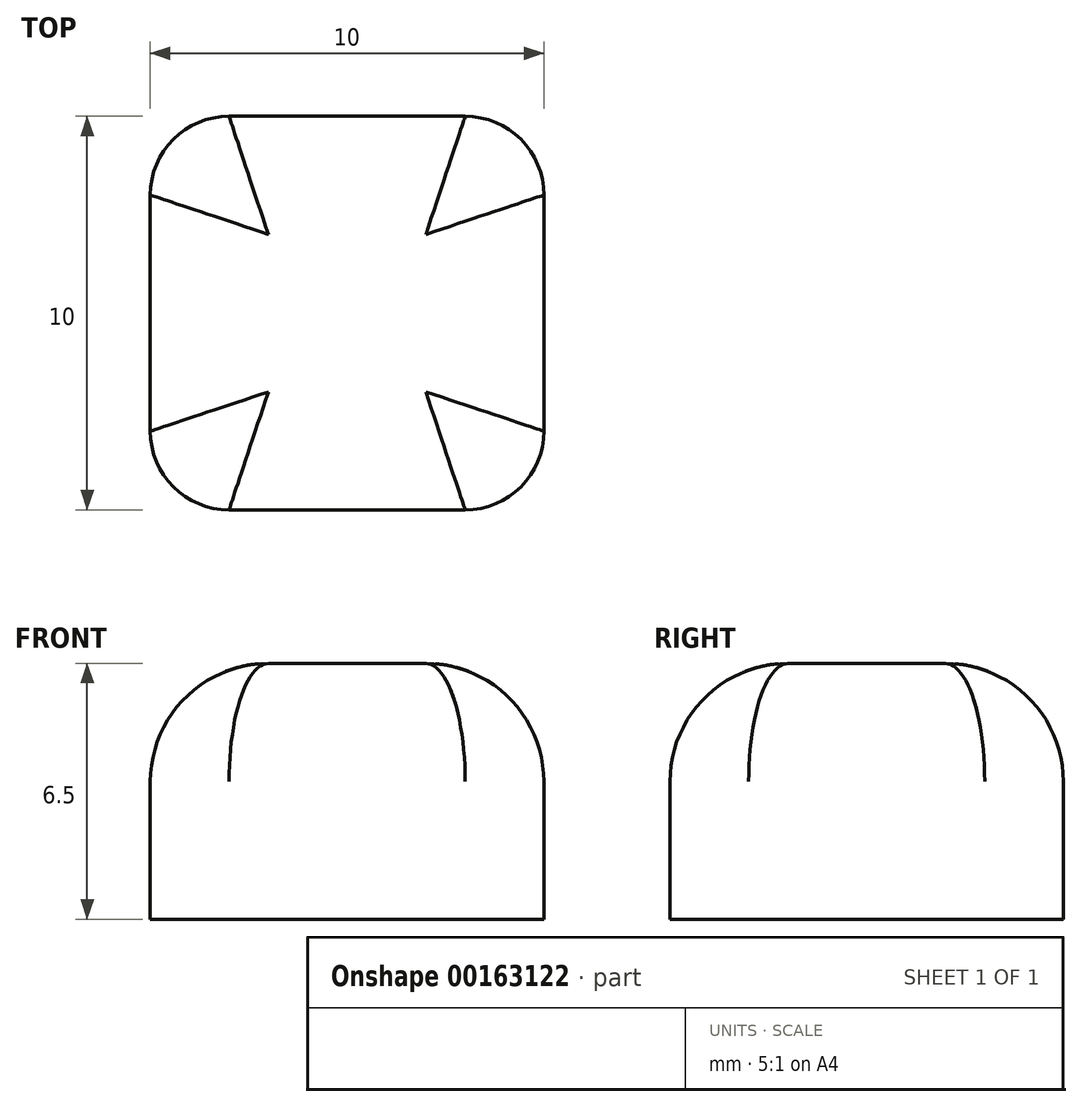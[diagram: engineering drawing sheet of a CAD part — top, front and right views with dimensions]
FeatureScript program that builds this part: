
annotation { "Feature Type Name" : "Feature", "Feature Type Description" : "" }
export const myFeature = defineFeature(function(context is Context, id is Id, definition is map)
    precondition{}
    {
        {
            var Q0;
            Q0=qCreatedBy(makeId("Top.planeOp"),FACE);
            var sketch = newSketch(context, id + "F0", { "sketchPlane" : qUnion([Q0])});
            skLineSegment(sketch, "E0.bottom", {"start": v(0, 0) * mm, "end": v(10, 0) * mm});
            skLineSegment(sketch, "E0.top", {"start": v(0, 10) * mm, "end": v(10, 10) * mm});
            skLineSegment(sketch, "E0.left", {"start": v(0, 0) * mm, "end": v(0, 10) * mm});
            skLineSegment(sketch, "E0.right", {"start": v(10, 0) * mm, "end": v(10, 10) * mm});
            skSolve(sketch);
        }
        {
            var Q0;
            Q0 = qSketchRegion(id + "F0", true);
            extrude(context, id + "F1", {"entities" : qUnion([Q0]), "depth" : 6.5 * mm});
        }
        {
            var Q0;
            Q0=makeQuery(id+"F1.opExtrude","SWEPT_EDGE",EDGE,{"disambiguationData":[OSD([sQuery(id+"F0.wireOp",EDGE,"E0.bottom"),sQuery(id+"F0.wireOp",EDGE,"E0.right")])]});
            var Q1;
            Q1=makeQuery(id+"F1.opExtrude","SWEPT_EDGE",EDGE,{"disambiguationData":[OSD([sQuery(id+"F0.wireOp",EDGE,"E0.bottom"),sQuery(id+"F0.wireOp",EDGE,"E0.left")])]});
            var Q2;
            Q2=makeQuery(id+"F1.opExtrude","SWEPT_EDGE",EDGE,{"disambiguationData":[OSD([sQuery(id+"F0.wireOp",EDGE,"E0.top"),sQuery(id+"F0.wireOp",EDGE,"E0.left")])]});
            var Q3;
            Q3=makeQuery(id+"F1.opExtrude","SWEPT_EDGE",EDGE,{"disambiguationData":[OSD([sQuery(id+"F0.wireOp",EDGE,"E0.top"),sQuery(id+"F0.wireOp",EDGE,"E0.right")])]});
            fillet(context, id + "F2", {"entities" : qUnion([Q0, Q1, Q2, Q3]), "radius" : 2 * mm, "tangentPropagation" : true, "allowEdgeOverflow" : false});
        }
        {
            var Q0;
            Q0=makeQuery(id+"F1.opExtrude","CAP_FACE",FACE,{"disambiguationData":[OSD([sQuery(id+"F0.wireOp",EDGE,"E0.bottom"),sQuery(id+"F0.wireOp",EDGE,"E0.top"),sQuery(id+"F0.wireOp",EDGE,"E0.left"),sQuery(id+"F0.wireOp",EDGE,"E0.right")])],"isStart":false});
            fillet(context, id + "F3", {"entities" : qUnion([Q0]), "radius" : 3 * mm, "tangentPropagation" : true, "allowEdgeOverflow" : false});
        }
    });
